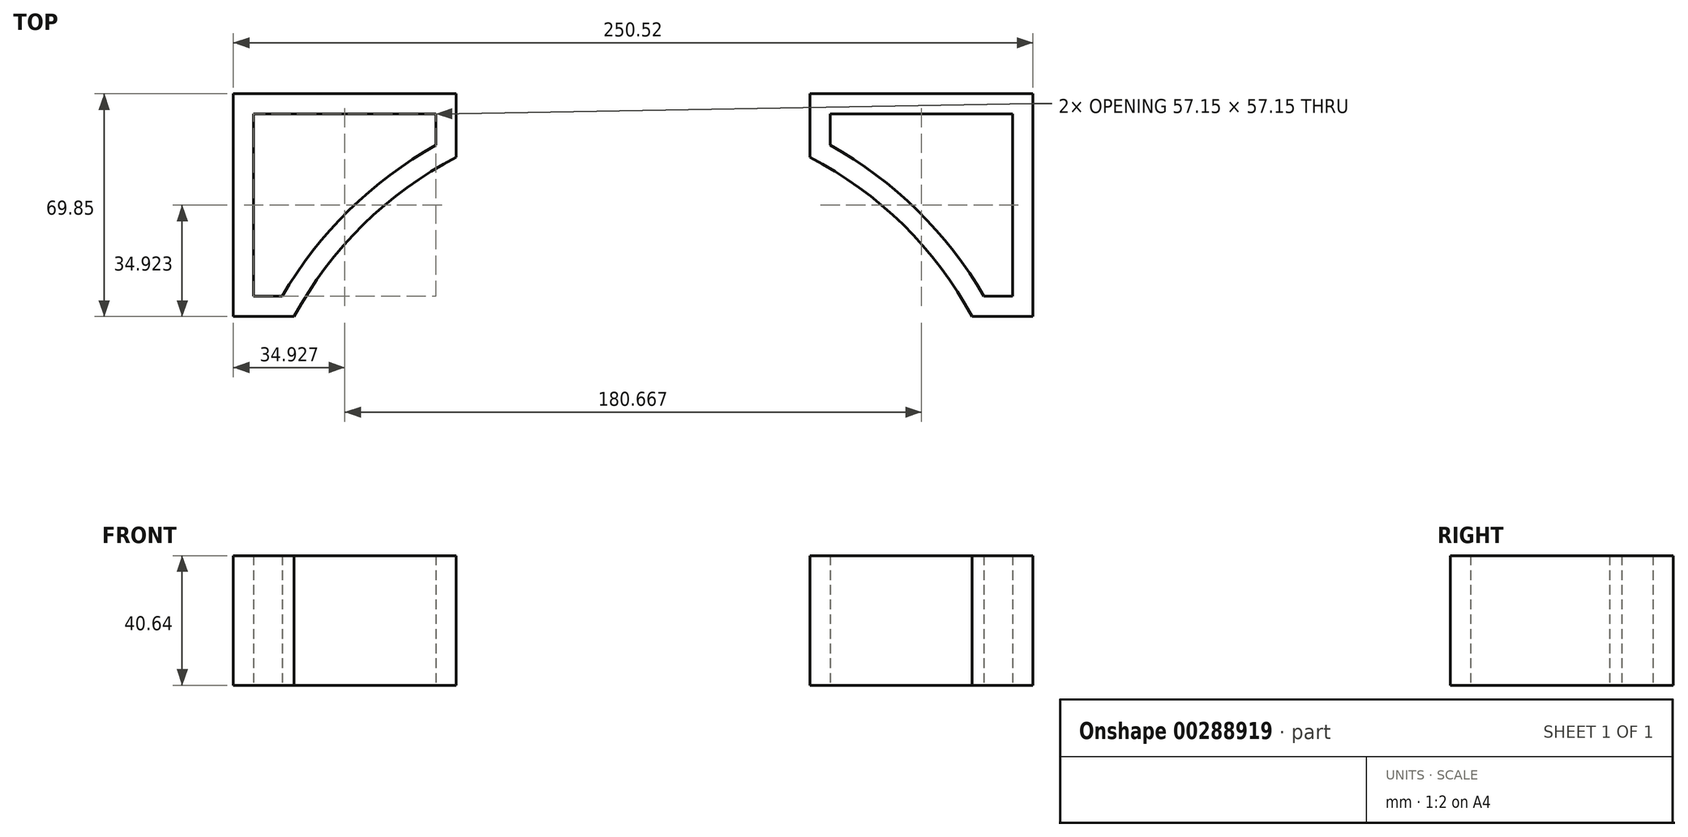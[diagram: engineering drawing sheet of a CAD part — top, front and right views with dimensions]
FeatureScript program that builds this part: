
annotation { "Feature Type Name" : "Feature", "Feature Type Description" : "" }
export const myFeature = defineFeature(function(context is Context, id is Id, definition is map)
    precondition{}
    {
        {
            var Q0;
            Q0=qCreatedBy(makeId("Top.planeOp"),FACE);
            var sketch = newSketch(context, id + "F0", { "sketchPlane" : qUnion([Q0])});
            skArc(sketch, "E0", {"start": v(-55.4, 107.17) * mm, "mid": v(-84.58, 86.04) * mm, "end": v(-106.2, 57.24) * mm});
            skLineSegment(sketch, "E1", {"start": v(-55.4, 107.17) * mm, "end": v(-55.4, 127.09) * mm});
            skLineSegment(sketch, "E2", {"start": v(-55.4, 127.09) * mm, "end": v(-125.26, 127.09) * mm});
            skLineSegment(sketch, "E3", {"start": v(-125.26, 127.09) * mm, "end": v(-125.26, 57.24) * mm});
            skLineSegment(sketch, "E4", {"start": v(-125.26, 57.24) * mm, "end": v(-106.2, 57.24) * mm});
            skLineSegment(sketch, "E5.0", {"start": v(-118.9, 120.74) * mm, "end": v(-118.9, 63.59) * mm});
            skLineSegment(sketch, "E5.1", {"start": v(-61.76, 120.74) * mm, "end": v(-118.9, 120.74) * mm});
            skLineSegment(sketch, "E5.2", {"start": v(-118.9, 63.59) * mm, "end": v(-109.93, 63.59) * mm});
            skArc(sketch, "E5.3", {"start": v(-61.76, 110.97) * mm, "mid": v(-89.06, 90.54) * mm, "end": v(-109.93, 63.59) * mm});
            skLineSegment(sketch, "E5.4", {"start": v(-61.76, 110.97) * mm, "end": v(-61.76, 120.74) * mm});
            skLineSegment(sketch, "E6.MirrorCS", {"start": v(61.76, 110.97) * mm, "end": v(61.76, 120.74) * mm});
            skLineSegment(sketch, "E7.MirrorCS", {"start": v(118.9, 63.59) * mm, "end": v(109.93, 63.59) * mm});
            skLineSegment(sketch, "E8.MirrorCS", {"start": v(125.26, 57.24) * mm, "end": v(106.2, 57.24) * mm});
            skArc(sketch, "E9.MirrorCS", {"start": v(61.76, 110.97) * mm, "mid": v(89.06, 90.54) * mm, "end": v(109.93, 63.59) * mm});
            skLineSegment(sketch, "E10.MirrorCS", {"start": v(61.76, 120.74) * mm, "end": v(118.9, 120.74) * mm});
            skLineSegment(sketch, "E11.MirrorCS", {"start": v(118.9, 120.74) * mm, "end": v(118.9, 63.59) * mm});
            skLineSegment(sketch, "E12.MirrorCS", {"start": v(125.26, 127.09) * mm, "end": v(125.26, 57.24) * mm});
            skLineSegment(sketch, "E13.MirrorCS", {"start": v(55.4, 107.17) * mm, "end": v(55.4, 127.09) * mm});
            skLineSegment(sketch, "E14.MirrorCS", {"start": v(55.4, 127.09) * mm, "end": v(125.26, 127.09) * mm});
            skArc(sketch, "E15.MirrorCS", {"start": v(55.4, 107.17) * mm, "mid": v(84.58, 86.04) * mm, "end": v(106.2, 57.24) * mm});
            skSolve(sketch);
        }
        {
            var Q0;
            Q0 = qSketchRegion(id + "F0", true);
            extrude(context, id + "F1", {"entities" : qUnion([Q0]), "depth" : 40.64 * mm});
        }
    });
